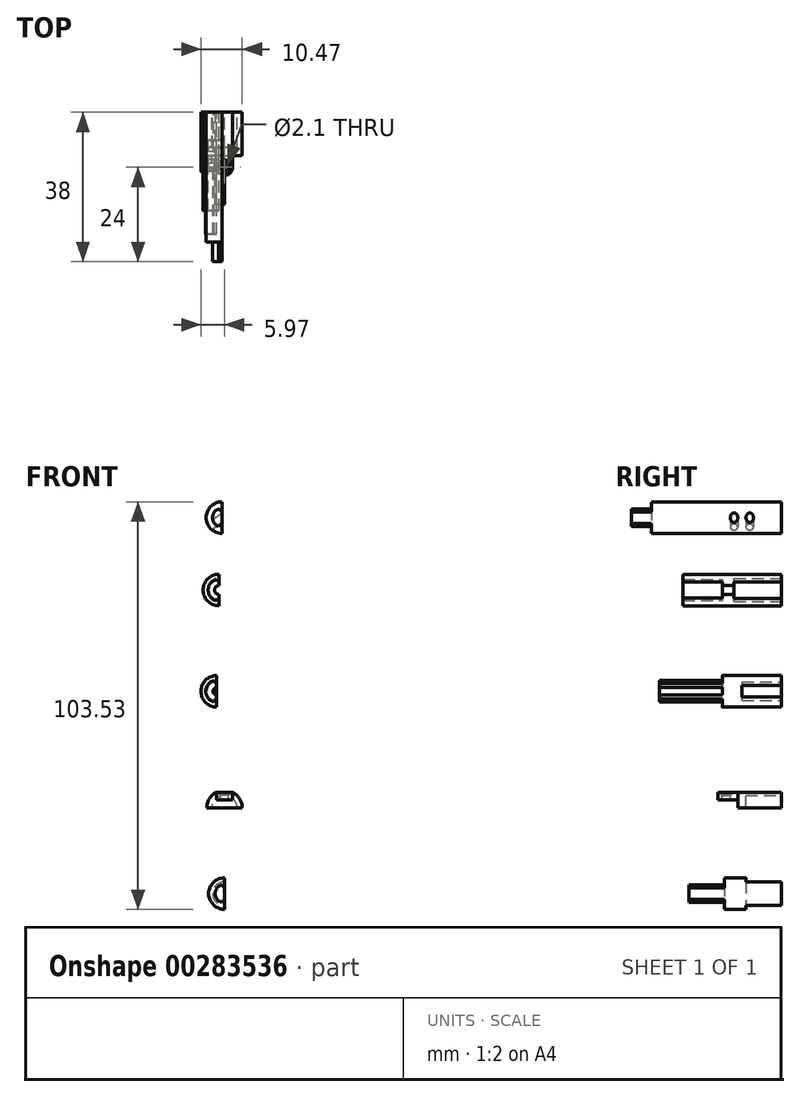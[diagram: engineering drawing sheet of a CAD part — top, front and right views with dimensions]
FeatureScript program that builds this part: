
annotation { "Feature Type Name" : "Feature", "Feature Type Description" : "" }
export const myFeature = defineFeature(function(context is Context, id is Id, definition is map)
    precondition{}
    {
        {
            var Q0;
            Q0=qCreatedBy(makeId("Front.planeOp"),FACE);
            var sketch = newSketch(context, id + "F0", { "sketchPlane" : qUnion([Q0])});
            skLineSegment(sketch, "E0", {"start": v(0, 4) * mm, "end": v(-2.06, 4) * mm});
            skLineSegment(sketch, "E1", {"start": v(-2.06, 4) * mm, "end": v(2.06, 4) * mm});
            skArc(sketch, "E2", {"start": v(-2.06, 4) * mm, "mid": v(-3.84, 2.34) * mm, "end": v(-4.5, 0) * mm});
            skArc(sketch, "E3", {"start": v(2.06, 4) * mm, "mid": v(3.84, 2.34) * mm, "end": v(4.5, 0) * mm});
            skLineSegment(sketch, "E4", {"start": v(-4.5, 0) * mm, "end": v(4.5, 0) * mm});
            skArc(sketch, "E5", {"start": v(3.2, 0) * mm, "mid": v(0, 3.2) * mm, "end": v(-3.2, 0) * mm});
            skSolve(sketch);
        }
        {
            var Q0;
            {var subQ0=sQuery(id+"F0.wireOp",EDGE,"E2");Q0=makeQuery(id+"F0.imprint","IMPRINT",FACE,{"disambiguationData":[TD([[makeQuery(id+"F0.imprint","IMPRINT",EDGE,{"derivedFrom":subQ0}),1.0]])]});}
            extrude(context, id + "F1", {"entities" : qUnion([Q0]), "depth" : 9 * mm});
        }
        {
            var Q0;
            Q0=makeQuery(id+"F1.opExtrude","CAP_FACE",FACE,{"disambiguationData":[OSD([sQuery(id+"F0.wireOp",EDGE,"E1"),sQuery(id+"F0.wireOp",EDGE,"E2"),sQuery(id+"F0.wireOp",EDGE,"E3"),sQuery(id+"F0.wireOp",EDGE,"E4"),sQuery(id+"F0.wireOp",EDGE,"E5")])],"isStart":false});
            var sketch = newSketch(context, id + "F2", { "sketchPlane" : qUnion([Q0])});
            skArc(sketch, "E6", {"start": v(-4.5, 0) * mm, "mid": v(-3.84, 2.34) * mm, "end": v(-2.06, 4) * mm});
            skArc(sketch, "E7", {"start": v(2.06, 4) * mm, "mid": v(3.84, 2.34) * mm, "end": v(4.5, 0) * mm});
            skLineSegment(sketch, "E8", {"start": v(-2.06, 4) * mm, "end": v(2.06, 4) * mm});
            skLineSegment(sketch, "E9", {"start": v(4.5, 0) * mm, "end": v(-4.5, 0) * mm});
            skSolve(sketch);
        }
        {
            var Q0;
            Q0 = qSketchRegion(id + "F2", true);
            extrude(context, id + "F3", {"entities" : qUnion([Q0]), "operationType" : NewBodyOperationType.ADD, "depth" : 2 * mm});
        }
        {
            var Q0;
            Q0=makeQuery(id+"F3.opExtrude","CAP_FACE",FACE,{"disambiguationData":[OSD([sQuery(id+"F2.wireOp",EDGE,"E6"),sQuery(id+"F2.wireOp",EDGE,"E7"),sQuery(id+"F2.wireOp",EDGE,"E8"),sQuery(id+"F2.wireOp",EDGE,"E9")])],"isStart":false});
            var sketch = newSketch(context, id + "F4", { "sketchPlane" : qUnion([Q0])});
            skLineSegment(sketch, "E10", {"start": v(-2.06, 4) * mm, "end": v(-2.06, 2.1) * mm});
            skLineSegment(sketch, "E11", {"start": v(-2.06, 2.1) * mm, "end": v(2.06, 2.1) * mm});
            skLineSegment(sketch, "E12", {"start": v(2.06, 2.1) * mm, "end": v(2.06, 4) * mm});
            skLineSegment(sketch, "E13", {"start": v(2.06, 4) * mm, "end": v(-2.06, 4) * mm});
            skSolve(sketch);
        }
        {
            var Q0;
            Q0=makeQuery(id+"F4.imprint","IMPRINT",FACE,{"disambiguationData":[TD([[makeQuery(id+"F4.imprint","IMPRINT",EDGE,{"derivedFrom":sQuery(id+"F4.wireOp",EDGE,"E10")}),1.0]])]});
            extrude(context, id + "F5", {"entities" : qUnion([Q0]), "operationType" : NewBodyOperationType.ADD, "depth" : 3 * mm});
        }
        {
            var Q0;
            Q0=makeQuery(id+"F5.opExtrude","CAP_FACE",FACE,{"disambiguationData":[OSD([sQuery(id+"F4.wireOp",EDGE,"E10"),sQuery(id+"F4.wireOp",EDGE,"E11"),sQuery(id+"F4.wireOp",EDGE,"E12"),sQuery(id+"F4.wireOp",EDGE,"E13")])],"isStart":false});
            var sketch = newSketch(context, id + "F6", { "sketchPlane" : qUnion([Q0])});
            skLineSegment(sketch, "E14", {"start": v(0, 2.1) * mm, "end": v(0, 4) * mm});
            skLineSegment(sketch, "E15", {"start": v(0, 4) * mm, "end": v(-2.06, 4) * mm});
            skLineSegment(sketch, "E16", {"start": v(-2.06, 4) * mm, "end": v(-2.06, 2.1) * mm});
            skLineSegment(sketch, "E17", {"start": v(-2.06, 2.1) * mm, "end": v(0, 2.1) * mm});
            skSolve(sketch);
        }
        {
            var Q0;
            Q0=makeQuery(id+"F6.imprint","IMPRINT",FACE,{"disambiguationData":[TD([[makeQuery(id+"F6.imprint","IMPRINT",EDGE,{"derivedFrom":sQuery(id+"F6.wireOp",EDGE,"E14")}),1.0]])]});
            var Q1;
            Q1=sQuery(id+"F6.wireOp",EDGE,"E14");
            revolve(context, id + "F7", {"operationType" : NewBodyOperationType.ADD, "entities" : qUnion([Q0]), "axis" : qUnion([Q1]), "revolveType" : RevolveType.FULL});
        }
        {
            var Q0;
            Q0=makeQuery(id+"F7.boolean.opBoolean","MERGE",FACE,{"derivedFrom":[makeQuery(id+"F5.boolean.opBoolean","MERGE",FACE,{"derivedFrom":[makeQuery(id+"F3.boolean.opBoolean","MERGE",FACE,{"derivedFrom":[makeQuery(id+"F1.opExtrude","SWEPT_FACE",FACE,{"disambiguationData":[OSD([sQuery(id+"F0.wireOp",EDGE,"E1")])]}),makeQuery(id+"F3.opExtrude","SWEPT_FACE",FACE,{"disambiguationData":[OSD([sQuery(id+"F2.wireOp",EDGE,"E8")])]})]}),makeQuery(id+"F5.opExtrude","SWEPT_FACE",FACE,{"disambiguationData":[OSD([sQuery(id+"F4.wireOp",EDGE,"E13")])]})]}),makeQuery(id+"F7.opRevolve","SWEPT_FACE",FACE,{"disambiguationData":[OSD([sQuery(id+"F6.wireOp",EDGE,"E15")])]})]});
            var sketch = newSketch(context, id + "F8", { "sketchPlane" : qUnion([Q0])});
            skCircle(sketch, "E18", {"center": v(0, -14) * mm, "radius": 1.05 * mm});
            skSolve(sketch);
        }
        {
            var Q0;
            Q0=makeQuery(id+"F8.imprint","IMPRINT",FACE,{"disambiguationData":[TD([[makeQuery(id+"F8.imprint","IMPRINT",EDGE,{"derivedFrom":sQuery(id+"F8.wireOp",EDGE,"E18")}),1.0]])]});
            extrude(context, id + "F9", {"entities" : qUnion([Q0]), "operationType" : NewBodyOperationType.REMOVE, "oppositeDirection" : true, "depth" : 2 * mm, "hasSecondDirection" : true, "secondDirectionOppositeDirection" : false, "secondDirectionDepth" : 25 * mm});
        }
        {
            var Q0;
            Q0=qCreatedBy(makeId("Front.planeOp"),FACE);
            var sketch = newSketch(context, id + "F10", { "sketchPlane" : qUnion([Q0])});
            skLineSegment(sketch, "E19", {"start": v(0, -24.77) * mm, "end": v(0, -18.77) * mm});
            skArc(sketch, "E20", {"start": v(0, -18.77) * mm, "mid": v(-3, -21.77) * mm, "end": v(0, -24.77) * mm});
            skSolve(sketch);
        }
        {
            var Q0;
            Q0=makeQuery(id+"F10.imprint","IMPRINT",FACE,{"disambiguationData":[TD([[makeQuery(id+"F10.imprint","IMPRINT",EDGE,{"derivedFrom":sQuery(id+"F10.wireOp",EDGE,"E19")}),1.0]])]});
            extrude(context, id + "F11", {"entities" : qUnion([Q0]), "depth" : 9 * mm});
        }
        {
            var Q0;
            Q0=makeQuery(id+"F11.opExtrude","CAP_FACE",FACE,{"disambiguationData":[OSD([sQuery(id+"F10.wireOp",EDGE,"E19"),sQuery(id+"F10.wireOp",EDGE,"E20")])],"isStart":false});
            var sketch = newSketch(context, id + "F12", { "sketchPlane" : qUnion([Q0])});
            skArc(sketch, "E21", {"start": v(0, -17.77) * mm, "mid": v(-4, -21.77) * mm, "end": v(0, -25.77) * mm});
            skLineSegment(sketch, "E22", {"start": v(0, -25.77) * mm, "end": v(0, -17.77) * mm});
            skSolve(sketch);
        }
        {
            var Q0;
            {var subQ0=sQuery(id+"F12.wireOp",EDGE,"E21");Q0=makeQuery(id+"F12.imprint","IMPRINT",FACE,{"disambiguationData":[TD([[makeQuery(id+"F12.imprint","IMPRINT",EDGE,{"derivedFrom":subQ0}),1.0]])]});}
            var Q1;
            {var subQ1=makeQuery(id+"F11.opExtrude","CAP_EDGE",EDGE,{"disambiguationData":[OSD([sQuery(id+"F10.wireOp",EDGE,"E20")])],"isStart":false});Q1=makeQuery(id+"F12.imprint","IMPRINT",FACE,{"disambiguationData":[TD([[makeQuery(id+"F12.imprint","IMPRINT",EDGE,{"derivedFrom":subQ1}),1.0]])]});}
            extrude(context, id + "F13", {"entities" : qUnion([Q0, Q1]), "operationType" : NewBodyOperationType.ADD, "depth" : 5.5 * mm});
        }
        {
            var Q0;
            Q0=makeQuery(id+"F13.opExtrude","CAP_FACE",FACE,{"disambiguationData":[OSD([sQuery(id+"F12.wireOp",EDGE,"E21"),sQuery(id+"F12.wireOp",EDGE,"E22")])],"isStart":false});
            var sketch = newSketch(context, id + "F14", { "sketchPlane" : qUnion([Q0])});
            skLineSegment(sketch, "E23", {"start": v(0, -21.77) * mm, "end": v(0, -23.2) * mm});
            skLineSegment(sketch, "E24", {"start": v(0, -23.2) * mm, "end": v(0, -20.34) * mm});
            skLineSegment(sketch, "E25", {"start": v(-0.8, -24) * mm, "end": v(0, -23.2) * mm});
            skLineSegment(sketch, "E26", {"start": v(-0.8, -19.54) * mm, "end": v(0, -20.34) * mm});
            skArc(sketch, "E27", {"start": v(-0.8, -24) * mm, "mid": v(-2.38, -21.77) * mm, "end": v(-0.8, -19.54) * mm});
            skSolve(sketch);
        }
        {
            var Q0;
            {var subQ0=sQuery(id+"F14.wireOp",EDGE,"E25");Q0=makeQuery(id+"F14.imprint","IMPRINT",FACE,{"disambiguationData":[TD([[makeQuery(id+"F14.imprint","IMPRINT",EDGE,{"derivedFrom":subQ0}),1.0]])]});}
            extrude(context, id + "F15", {"entities" : qUnion([Q0]), "operationType" : NewBodyOperationType.ADD, "depth" : 9 * mm});
        }
        {
            var Q0;
            Q0=qCreatedBy(makeId("Front.planeOp"),FACE);
            var sketch = newSketch(context, id + "F16", { "sketchPlane" : qUnion([Q0])});
            skLineSegment(sketch, "E28", {"start": v(-2.83, 27.29) * mm, "end": v(-1.97, 28.16) * mm});
            skLineSegment(sketch, "E29", {"start": v(-2.83, 31.98) * mm, "end": v(-1.97, 31.1) * mm});
            skArc(sketch, "E30", {"start": v(-2.83, 27.29) * mm, "mid": v(-4.47, 29.63) * mm, "end": v(-2.83, 31.98) * mm});
            skArc(sketch, "E31", {"start": v(-1.97, 25.63) * mm, "mid": v(-5.97, 29.63) * mm, "end": v(-1.97, 33.63) * mm});
            skLineSegment(sketch, "E32", {"start": v(-1.97, 28.16) * mm, "end": v(-1.97, 25.63) * mm});
            skLineSegment(sketch, "E33", {"start": v(-1.97, 31.1) * mm, "end": v(-1.97, 33.63) * mm});
            skSolve(sketch);
        }
        {
            var Q0;
            Q0=makeQuery(id+"F16.imprint","IMPRINT",FACE,{"disambiguationData":[TD([[makeQuery(id+"F16.imprint","IMPRINT",EDGE,{"derivedFrom":sQuery(id+"F16.wireOp",EDGE,"E28")}),-1.0]])]});
            extrude(context, id + "F17", {"entities" : qUnion([Q0]), "depth" : 10 * mm});
        }
        {
            var Q0;
            Q0=makeQuery(id+"F17.opExtrude","CAP_FACE",FACE,{"disambiguationData":[OSD([sQuery(id+"F16.wireOp",EDGE,"E28"),sQuery(id+"F16.wireOp",EDGE,"E29"),sQuery(id+"F16.wireOp",EDGE,"E30"),sQuery(id+"F16.wireOp",EDGE,"E31"),sQuery(id+"F16.wireOp",EDGE,"E32"),sQuery(id+"F16.wireOp",EDGE,"E33")])],"isStart":false});
            var sketch = newSketch(context, id + "F18", { "sketchPlane" : qUnion([Q0])});
            skLineSegment(sketch, "E34", {"start": v(-1.97, 28.16) * mm, "end": v(-1.97, 31.1) * mm});
            skSolve(sketch);
        }
        {
            var Q0;
            Q0=makeQuery(id+"F18.imprint","IMPRINT",FACE,{"disambiguationData":[TD([[makeQuery(id+"F18.imprint","IMPRINT",EDGE,{"derivedFrom":sQuery(id+"F18.wireOp",EDGE,"E34")}),1.0]])]});
            var Q1;
            Q1=makeQuery(id+"F18.imprint","IMPRINT",FACE,{"disambiguationData":[TD([[makeQuery(id+"F18.imprint","IMPRINT",EDGE,{"derivedFrom":makeQuery(id+"F17.opExtrude","CAP_EDGE",EDGE,{"disambiguationData":[OSD([sQuery(id+"F16.wireOp",EDGE,"E28")])],"isStart":false})}),-1.0]])]});
            extrude(context, id + "F19", {"entities" : qUnion([Q0, Q1]), "operationType" : NewBodyOperationType.ADD, "depth" : 5 * mm});
        }
        {
            var Q0;
            Q0=makeQuery(id+"F19.opExtrude","CAP_FACE",FACE,{"disambiguationData":[OSD([sQuery(id+"F16.wireOp",EDGE,"E31"),sQuery(id+"F16.wireOp",EDGE,"E32"),sQuery(id+"F16.wireOp",EDGE,"E33"),sQuery(id+"F18.wireOp",EDGE,"E34")])],"isStart":false});
            var sketch = newSketch(context, id + "F20", { "sketchPlane" : qUnion([Q0])});
            skLineSegment(sketch, "E35", {"start": v(-2.67, 32.34) * mm, "end": v(-1.97, 31.63) * mm});
            skLineSegment(sketch, "E36", {"start": v(-2.67, 26.92) * mm, "end": v(-1.97, 27.63) * mm});
            skLineSegment(sketch, "E37", {"start": v(-1.97, 27.63) * mm, "end": v(-1.97, 31.63) * mm});
            skArc(sketch, "E38", {"start": v(-2.67, 26.92) * mm, "mid": v(-4.77, 29.63) * mm, "end": v(-2.67, 32.34) * mm});
            skArc(sketch, "E39", {"start": v(-1.97, 28.68) * mm, "mid": v(-2.92, 29.63) * mm, "end": v(-1.97, 30.58) * mm});
            skSolve(sketch);
        }
        {
            var Q0;
            {var subQ1=sQuery(id+"F20.wireOp",EDGE,"E35");Q0=makeQuery(id+"F20.imprint","IMPRINT",FACE,{"disambiguationData":[TD([[makeQuery(id+"F20.imprint","IMPRINT",EDGE,{"derivedFrom":subQ1}),-1.0]])]});}
            extrude(context, id + "F21", {"entities" : qUnion([Q0]), "operationType" : NewBodyOperationType.ADD, "depth" : 16 * mm});
        }
        {
            var Q0;
            Q0=qCreatedBy(makeId("Front.planeOp"),FACE);
            var sketch = newSketch(context, id + "F22", { "sketchPlane" : qUnion([Q0])});
            skLineSegment(sketch, "E40", {"start": v(-2.23, 52.47) * mm, "end": v(-1.44, 53.26) * mm});
            skLineSegment(sketch, "E41", {"start": v(-1.44, 57.46) * mm, "end": v(-2.23, 58.25) * mm});
            skArc(sketch, "E42", {"start": v(-1.44, 51.36) * mm, "mid": v(-5.44, 55.36) * mm, "end": v(-1.44, 59.36) * mm});
            skArc(sketch, "E43", {"start": v(-2.23, 52.47) * mm, "mid": v(-4.44, 55.36) * mm, "end": v(-2.23, 58.25) * mm});
            skLineSegment(sketch, "E44", {"start": v(-1.44, 51.36) * mm, "end": v(-1.44, 53.26) * mm});
            skLineSegment(sketch, "E45", {"start": v(-1.44, 57.46) * mm, "end": v(-1.44, 59.36) * mm});
            skSolve(sketch);
        }
        {
            var Q0;
            Q0=makeQuery(id+"F22.imprint","IMPRINT",FACE,{"disambiguationData":[TD([[makeQuery(id+"F22.imprint","IMPRINT",EDGE,{"derivedFrom":sQuery(id+"F22.wireOp",EDGE,"E40")}),-1.0]])]});
            extrude(context, id + "F23", {"entities" : qUnion([Q0]), "depth" : 12 * mm});
        }
        {
            var Q0;
            Q0=makeQuery(id+"F23.opExtrude","CAP_FACE",FACE,{"disambiguationData":[OSD([sQuery(id+"F22.wireOp",EDGE,"E40"),sQuery(id+"F22.wireOp",EDGE,"E41"),sQuery(id+"F22.wireOp",EDGE,"E42"),sQuery(id+"F22.wireOp",EDGE,"E43"),sQuery(id+"F22.wireOp",EDGE,"E44"),sQuery(id+"F22.wireOp",EDGE,"E45")])],"isStart":false});
            var sketch = newSketch(context, id + "F24", { "sketchPlane" : qUnion([Q0])});
            skLineSegment(sketch, "E46", {"start": v(-1.44, 53.26) * mm, "end": v(-1.44, 57.46) * mm});
            skLineSegment(sketch, "E47", {"start": v(-1.44, 55.36) * mm, "end": v(-1.44, 54.26) * mm});
            skArc(sketch, "E48", {"start": v(-1.44, 54.26) * mm, "mid": v(-2.54, 55.36) * mm, "end": v(-1.44, 56.46) * mm});
            skSolve(sketch);
        }
        {
            var Q0;
            Q0=makeQuery(id+"F24.imprint","IMPRINT",FACE,{"disambiguationData":[TD([[makeQuery(id+"F24.imprint","IMPRINT",EDGE,{"derivedFrom":sQuery(id+"F24.wireOp",EDGE,"E46")}),1.0]])]});
            var Q1;
            Q1=makeQuery(id+"F24.imprint","IMPRINT",FACE,{"disambiguationData":[TD([[makeQuery(id+"F24.imprint","IMPRINT",EDGE,{"derivedFrom":makeQuery(id+"F23.opExtrude","CAP_EDGE",EDGE,{"disambiguationData":[OSD([sQuery(id+"F22.wireOp",EDGE,"E40")])],"isStart":false})}),-1.0]])]});
            extrude(context, id + "F25", {"entities" : qUnion([Q0, Q1]), "operationType" : NewBodyOperationType.ADD, "depth" : 3 * mm});
        }
        {
            var Q0;
            Q0=makeQuery(id+"F25.opExtrude","CAP_FACE",FACE,{"disambiguationData":[OSD([sQuery(id+"F22.wireOp",EDGE,"E42"),sQuery(id+"F22.wireOp",EDGE,"E44"),sQuery(id+"F22.wireOp",EDGE,"E45"),sQuery(id+"F24.wireOp",EDGE,"E46")])],"isStart":false});
            var sketch = newSketch(context, id + "F26", { "sketchPlane" : qUnion([Q0])});
            skLineSegment(sketch, "E49", {"start": v(-1.44, 57.36) * mm, "end": v(-1.44, 53.36) * mm});
            skLineSegment(sketch, "E50", {"start": v(-1.44, 53.36) * mm, "end": v(-1.44, 57.36) * mm});
            skLineSegment(sketch, "E51", {"start": v(-2.07, 52.73) * mm, "end": v(-1.44, 53.36) * mm});
            skLineSegment(sketch, "E52", {"start": v(-2.07, 58) * mm, "end": v(-1.44, 57.36) * mm});
            skArc(sketch, "E53", {"start": v(-2.07, 52.73) * mm, "mid": v(-4.15, 55.36) * mm, "end": v(-2.07, 58) * mm});
            skSolve(sketch);
        }
        {
            var Q0;
            {var subQ3=sQuery(id+"F26.wireOp",EDGE,"E51");Q0=makeQuery(id+"F26.imprint","IMPRINT",FACE,{"disambiguationData":[TD([[makeQuery(id+"F26.imprint","IMPRINT",EDGE,{"derivedFrom":subQ3}),-1.0]])]});}
            extrude(context, id + "F27", {"entities" : qUnion([Q0]), "operationType" : NewBodyOperationType.ADD, "depth" : 10 * mm});
        }
        {
            var Q0;
            Q0=qCreatedBy(makeId("Front.planeOp"),FACE);
            var sketch = newSketch(context, id + "F28", { "sketchPlane" : qUnion([Q0])});
            skLineSegment(sketch, "E54", {"start": v(-0.65, 73.76) * mm, "end": v(-0.65, 72.33) * mm});
            skLineSegment(sketch, "E55", {"start": v(-0.65, 72.33) * mm, "end": v(-0.65, 75.18) * mm});
            skLineSegment(sketch, "E56", {"start": v(-1.46, 71.52) * mm, "end": v(-0.65, 72.33) * mm});
            skLineSegment(sketch, "E57", {"start": v(-1.46, 76) * mm, "end": v(-0.65, 75.18) * mm});
            skArc(sketch, "E58", {"start": v(-1.46, 71.52) * mm, "mid": v(-3.03, 73.76) * mm, "end": v(-1.46, 76) * mm});
            skArc(sketch, "E59", {"start": v(-0.65, 69.76) * mm, "mid": v(-4.65, 73.76) * mm, "end": v(-0.65, 77.76) * mm});
            skLineSegment(sketch, "E60", {"start": v(-0.65, 69.76) * mm, "end": v(-0.65, 77.76) * mm});
            skSolve(sketch);
        }
        {
            var Q0;
            {var subQ0=sQuery(id+"F28.wireOp",EDGE,"E56");Q0=makeQuery(id+"F28.imprint","IMPRINT",FACE,{"disambiguationData":[TD([[makeQuery(id+"F28.imprint","IMPRINT",EDGE,{"derivedFrom":subQ0}),1.0]])]});}
            var Q1;
            {var subQ2=sQuery(id+"F28.wireOp",EDGE,"E56");Q1=makeQuery(id+"F28.imprint","IMPRINT",FACE,{"disambiguationData":[TD([[makeQuery(id+"F28.imprint","IMPRINT",EDGE,{"derivedFrom":subQ2}),-1.0]])]});}
            extrude(context, id + "F29", {"entities" : qUnion([Q0, Q1]), "depth" : 33 * mm, "offsetDistance" : 25 * mm});
        }
        {
            var Q0;
            Q0=makeQuery(id+"F29.opExtrude","CAP_FACE",FACE,{"disambiguationData":[OSD([sQuery(id+"F28.wireOp",EDGE,"E59"),sQuery(id+"F28.wireOp",EDGE,"E60")])],"isStart":false});
            var sketch = newSketch(context, id + "F30", { "sketchPlane" : qUnion([Q0])});
            skLineSegment(sketch, "E61", {"start": v(-1.46, 71.52) * mm, "end": v(-0.65, 72.33) * mm});
            skLineSegment(sketch, "E62", {"start": v(-1.46, 76) * mm, "end": v(-0.65, 75.18) * mm});
            skArc(sketch, "E63", {"start": v(-1.46, 71.52) * mm, "mid": v(-3.03, 73.76) * mm, "end": v(-1.46, 76) * mm});
            skSolve(sketch);
        }
        {
            var Q0;
            {var subQ0=sQuery(id+"F30.wireOp",EDGE,"E61");Q0=makeQuery(id+"F30.imprint","IMPRINT",FACE,{"disambiguationData":[TD([[makeQuery(id+"F30.imprint","IMPRINT",EDGE,{"derivedFrom":subQ0}),1.0]])]});}
            extrude(context, id + "F31", {"entities" : qUnion([Q0]), "operationType" : NewBodyOperationType.ADD, "depth" : 5 * mm});
        }
        {
            var Q0;
            Q0=makeQuery(id+"F9.boolean.opBoolean","INTERSECT",EDGE,{"derivedFrom":[makeQuery(id+"F7.boolean.opBoolean","MERGE",FACE,{"derivedFrom":[makeQuery(id+"F5.boolean.opBoolean","MERGE",FACE,{"derivedFrom":[makeQuery(id+"F3.boolean.opBoolean","MERGE",FACE,{"derivedFrom":[makeQuery(id+"F1.opExtrude","SWEPT_FACE",FACE,{"disambiguationData":[OSD([sQuery(id+"F0.wireOp",EDGE,"E1")])]}),makeQuery(id+"F3.opExtrude","SWEPT_FACE",FACE,{"disambiguationData":[OSD([sQuery(id+"F2.wireOp",EDGE,"E8")])]})]}),makeQuery(id+"F5.opExtrude","SWEPT_FACE",FACE,{"disambiguationData":[OSD([sQuery(id+"F4.wireOp",EDGE,"E13")])]})]}),makeQuery(id+"F7.opRevolve","SWEPT_FACE",FACE,{"disambiguationData":[OSD([sQuery(id+"F6.wireOp",EDGE,"E15")])]})]}),makeQuery(id+"F9.opExtrude","SWEPT_FACE",FACE,{"disambiguationData":[OSD([sQuery(id+"F8.wireOp",EDGE,"E18")])]})]});
            chamfer(context, id + "F32", {"entities" : qUnion([Q0]), "width" : 0.8 * mm, "tangentPropagation" : true});
        }
        {
            var Q0;
            {var subQ0=sQuery(id+"F28.wireOp",EDGE,"E60");Q0=makeQuery(id+"F31.boolean.opBoolean","MERGE",FACE,{"derivedFrom":[makeQuery(id+"F29.opExtrude","SWEPT_FACE",FACE,{"disambiguationData":[OSD([subQ0])]}),makeQuery(id+"F31.opExtrude","SWEPT_FACE",FACE,{"disambiguationData":[OSD([subQ0])]})]});}
            var sketch = newSketch(context, id + "F33", { "sketchPlane" : qUnion([Q0])});
            skLineSegment(sketch, "E64", {"start": v(0, 73.76) * mm, "end": v(-38, 73.76) * mm});
            skSolve(sketch);
        }
        {
            var Q0;
            Q0=sQuery(id+"F33.wireOp",EDGE,"E64");
            cPlane(context, id + "F34", {"entities" : qUnion([Q0]), "cplaneType" : CPlaneType.LINE_ANGLE, "offset" : 25 * mm, "angle" : 307.5 * degree, "width" : 150 * mm, "height" : 150 * mm});
        }
        {
            var Q0;
            Q0=qCreatedBy(id+"F34.planeOp",FACE);
            var sketch = newSketch(context, id + "F35", { "sketchPlane" : qUnion([Q0])});
            skLineSegment(sketch, "E65", {"start": v(0, 58.91) * mm, "end": v(8, 58.91) * mm, "construction": true});
            skLineSegment(sketch, "E66", {"start": v(8, 58.91) * mm, "end": v(12, 58.91) * mm, "construction": true});
            skCircle(sketch, "E67", {"center": v(8, 58.91) * mm, "radius": 0.95 * mm});
            skCircle(sketch, "E68", {"center": v(12, 58.91) * mm, "radius": 0.95 * mm});
            skSolve(sketch);
        }
        {
            var Q0;
            Q0=makeQuery(id+"F35.imprint","IMPRINT",FACE,{"disambiguationData":[TD([[makeQuery(id+"F35.imprint","IMPRINT",EDGE,{"derivedFrom":sQuery(id+"F35.wireOp",EDGE,"E67")}),1.0]])]});
            var Q1;
            Q1=makeQuery(id+"F35.imprint","IMPRINT",FACE,{"disambiguationData":[TD([[makeQuery(id+"F35.imprint","IMPRINT",EDGE,{"derivedFrom":sQuery(id+"F35.wireOp",EDGE,"E68")}),1.0]])]});
            extrude(context, id + "F36", {"entities" : qUnion([Q0, Q1]), "operationType" : NewBodyOperationType.REMOVE, "oppositeDirection" : true, "depth" : 25 * mm, "symmetric" : true});
        }
    });
